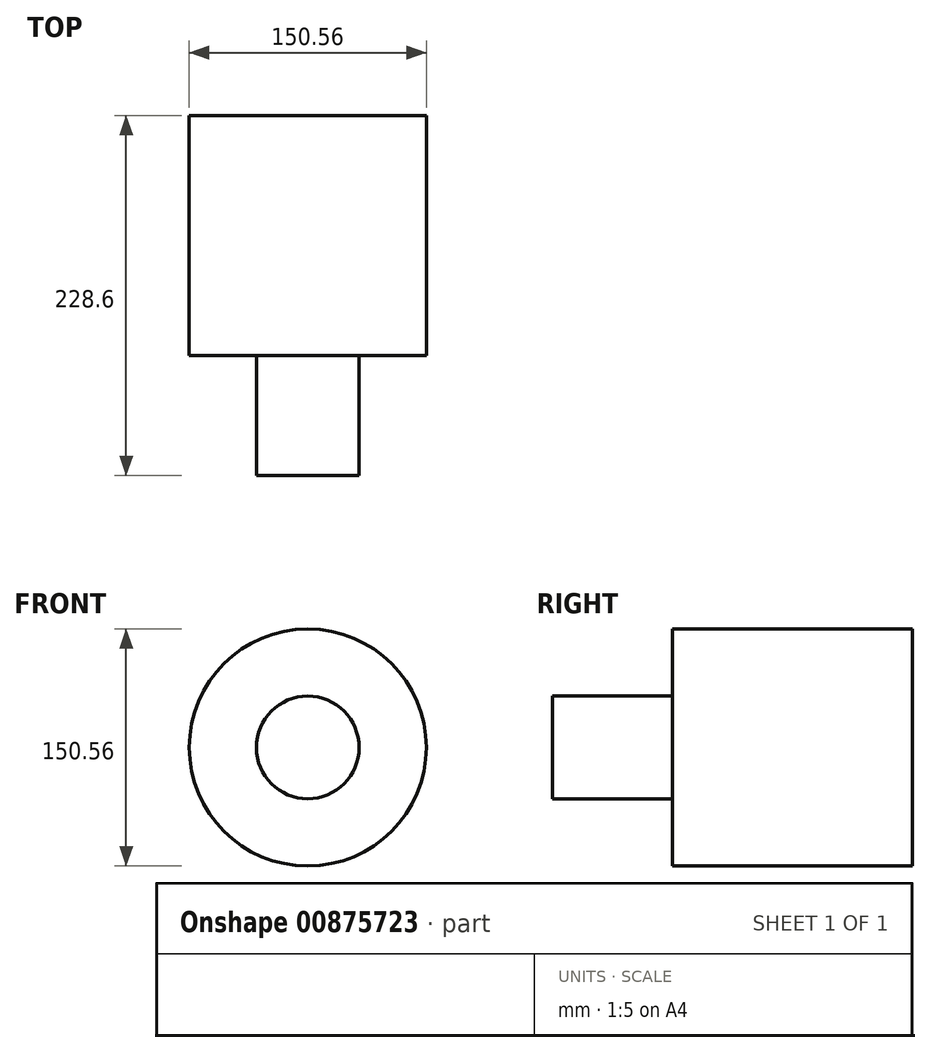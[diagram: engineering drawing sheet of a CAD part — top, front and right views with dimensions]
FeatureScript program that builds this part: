
annotation { "Feature Type Name" : "Feature", "Feature Type Description" : "" }
export const myFeature = defineFeature(function(context is Context, id is Id, definition is map)
    precondition{}
    {
        {
            var Q0;
            Q0=qCreatedBy(makeId("Front.planeOp"),FACE);
            var sketch = newSketch(context, id + "F0", { "sketchPlane" : qUnion([Q0])});
            skCircle(sketch, "E0", {"center": v(0, 0) * mm, "radius": 75.28 * mm});
            skSolve(sketch);
        }
        {
            var Q0;
            Q0=makeQuery(id+"F0.imprint","IMPRINT",FACE,{"disambiguationData":[TD([[makeQuery(id+"F0.imprint","IMPRINT",EDGE,{"derivedFrom":sQuery(id+"F0.wireOp",EDGE,"E0")}),1.0]])]});
            var sketch = newSketch(context, id + "F1", { "sketchPlane" : qUnion([Q0])});
            skCircle(sketch, "E1", {"center": v(0, 0) * mm, "radius": 32.6 * mm});
            skSolve(sketch);
        }
        {
            var Q0;
            Q0=makeQuery(id+"F1.imprint","IMPRINT",FACE,{"disambiguationData":[TD([[makeQuery(id+"F1.imprint","IMPRINT",EDGE,{"derivedFrom":sQuery(id+"F1.wireOp",EDGE,"E1")}),1.0]])]});
            var sketch = newSketch(context, id + "F2", { "sketchPlane" : qUnion([Q0])});
            skSolve(sketch);
        }
        {
            var Q0;
            Q0=makeQuery(id+"F2.imprint","IMPRINT",FACE,{"disambiguationData":[TD([[makeQuery(id+"F2.imprint","IMPRINT",EDGE,{"derivedFrom":makeQuery(id+"F1.imprint","IMPRINT",EDGE,{"derivedFrom":sQuery(id+"F1.wireOp",EDGE,"E1")})}),1.0]])]});
            extrude(context, id + "F3", {"entities" : qUnion([Q0]), "depth" : 76.2 * mm, "offsetDistance" : 25.4 * mm});
        }
        {
            var Q0;
            Q0=makeQuery(id+"F0.imprint","IMPRINT",FACE,{"disambiguationData":[TD([[makeQuery(id+"F0.imprint","IMPRINT",EDGE,{"derivedFrom":sQuery(id+"F0.wireOp",EDGE,"E0")}),1.0]])]});
            extrude(context, id + "F4", {"entities" : qUnion([Q0]), "operationType" : NewBodyOperationType.ADD, "oppositeDirection" : true, "depth" : 152.4 * mm, "offsetDistance" : 25.4 * mm});
        }
    });
